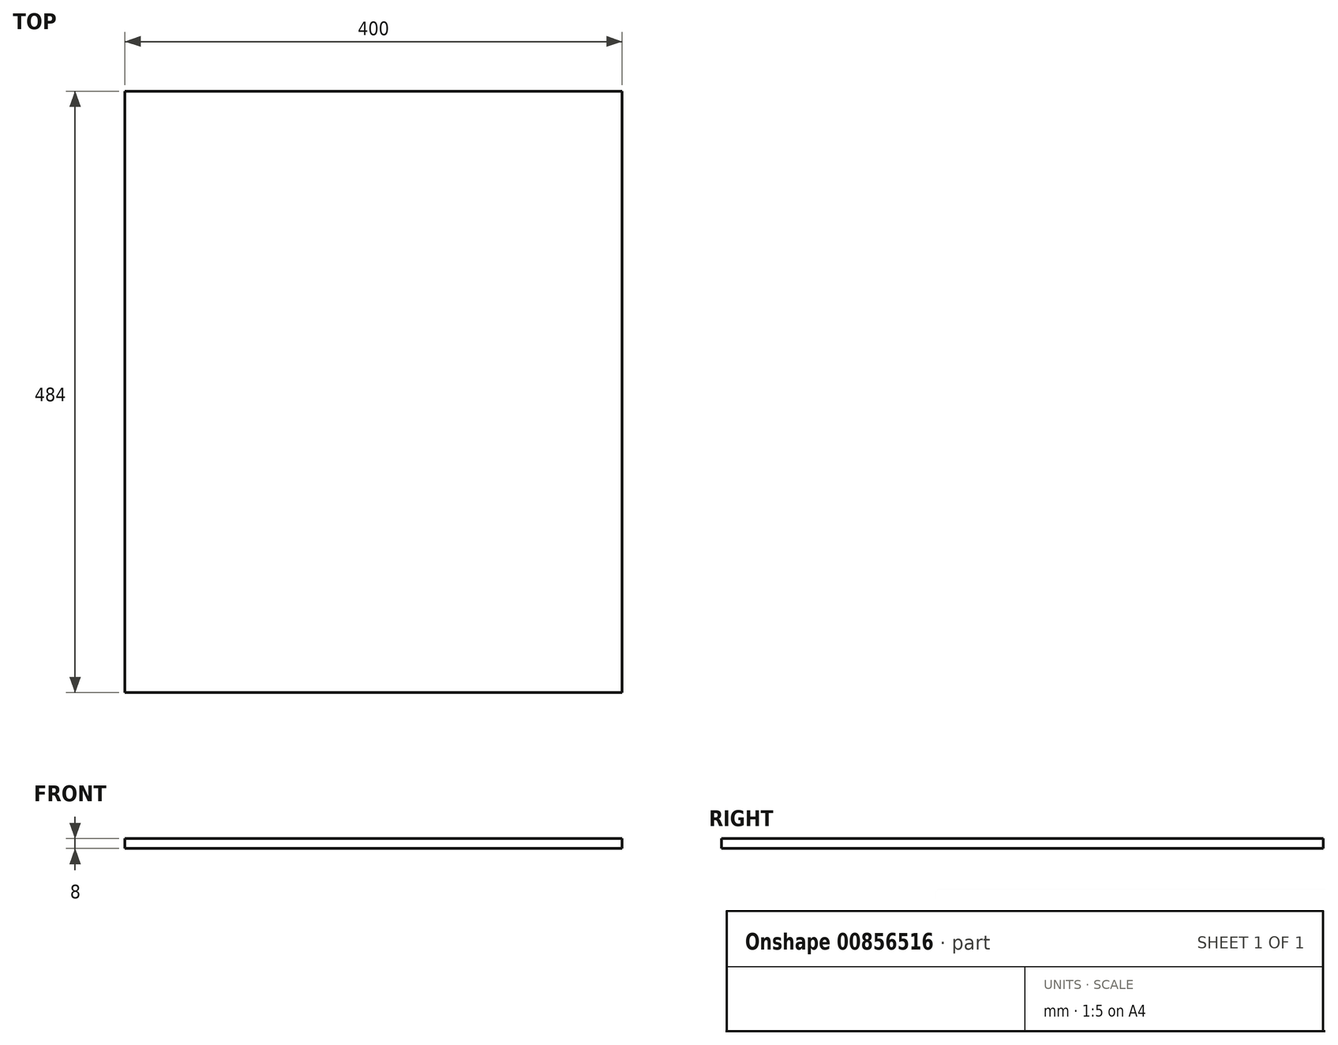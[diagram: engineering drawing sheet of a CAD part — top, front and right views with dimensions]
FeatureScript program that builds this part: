
annotation { "Feature Type Name" : "Feature", "Feature Type Description" : "" }
export const myFeature = defineFeature(function(context is Context, id is Id, definition is map)
    precondition{}
    {
        {
            var Q0;
            Q0=qCreatedBy(makeId("Top.planeOp"),FACE);
            var sketch = newSketch(context, id + "F0", { "sketchPlane" : qUnion([Q0])});
            skLineSegment(sketch, "E0.bottom", {"start": v(-200, 242) * mm, "end": v(200, 242) * mm});
            skLineSegment(sketch, "E0.top", {"start": v(-200, -242) * mm, "end": v(200, -242) * mm});
            skLineSegment(sketch, "E0.left", {"start": v(-200, 242) * mm, "end": v(-200, -242) * mm});
            skLineSegment(sketch, "E0.right", {"start": v(200, 242) * mm, "end": v(200, -242) * mm});
            skPoint(sketch, "E0.middle", {"position": v(0, 0) * mm});
            skSolve(sketch);
        }
        {
            var Q0;
            Q0=makeQuery(id+"F0.imprint","IMPRINT",FACE,{"disambiguationData":[TD([[makeQuery(id+"F0.imprint","IMPRINT",EDGE,{"derivedFrom":sQuery(id+"F0.wireOp",EDGE,"E0.bottom")}),-1.0]])]});
            extrude(context, id + "F1", {"entities" : qUnion([Q0]), "depth" : 8 * mm, "offsetDistance" : 25 * mm});
        }
    });
